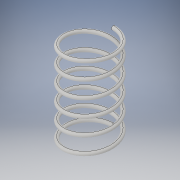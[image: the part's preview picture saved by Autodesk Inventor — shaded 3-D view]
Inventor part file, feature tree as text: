
AUTODESK INVENTOR PART (.ipt)
format: ipt  version: 2019 (Build 230136000, 136)  size: 439,296 bytes
history: native  units: in
note: dims shown in document units (in); Inventor stores cm internally (conversion verified against a paired STEP export)
features: helix x1, sketch x1
ambient origin geometry x8: Origin, YZ Plane, XZ Plane, XY Plane, X Axis, Y Axis, Z Axis, Center Point
bodies: Solid1 (feature_tree)
feature tree (2):
  helix  "Coil1"  [1 undecoded]
  sketch  "Sketch1"  dims[d1=0.0787in d2=1.7717in d3=0.3937in d4=1.7717in d5=1.9685in d6=0.0in d7=90.0deg d8=90.0deg d9=90.0deg d10=90.0deg]
note: 1 required parameter value undecoded (feature->parameter linkage not recoverable at this tier; creation-order binding heuristic only, values carry confidence <= 0.55)
